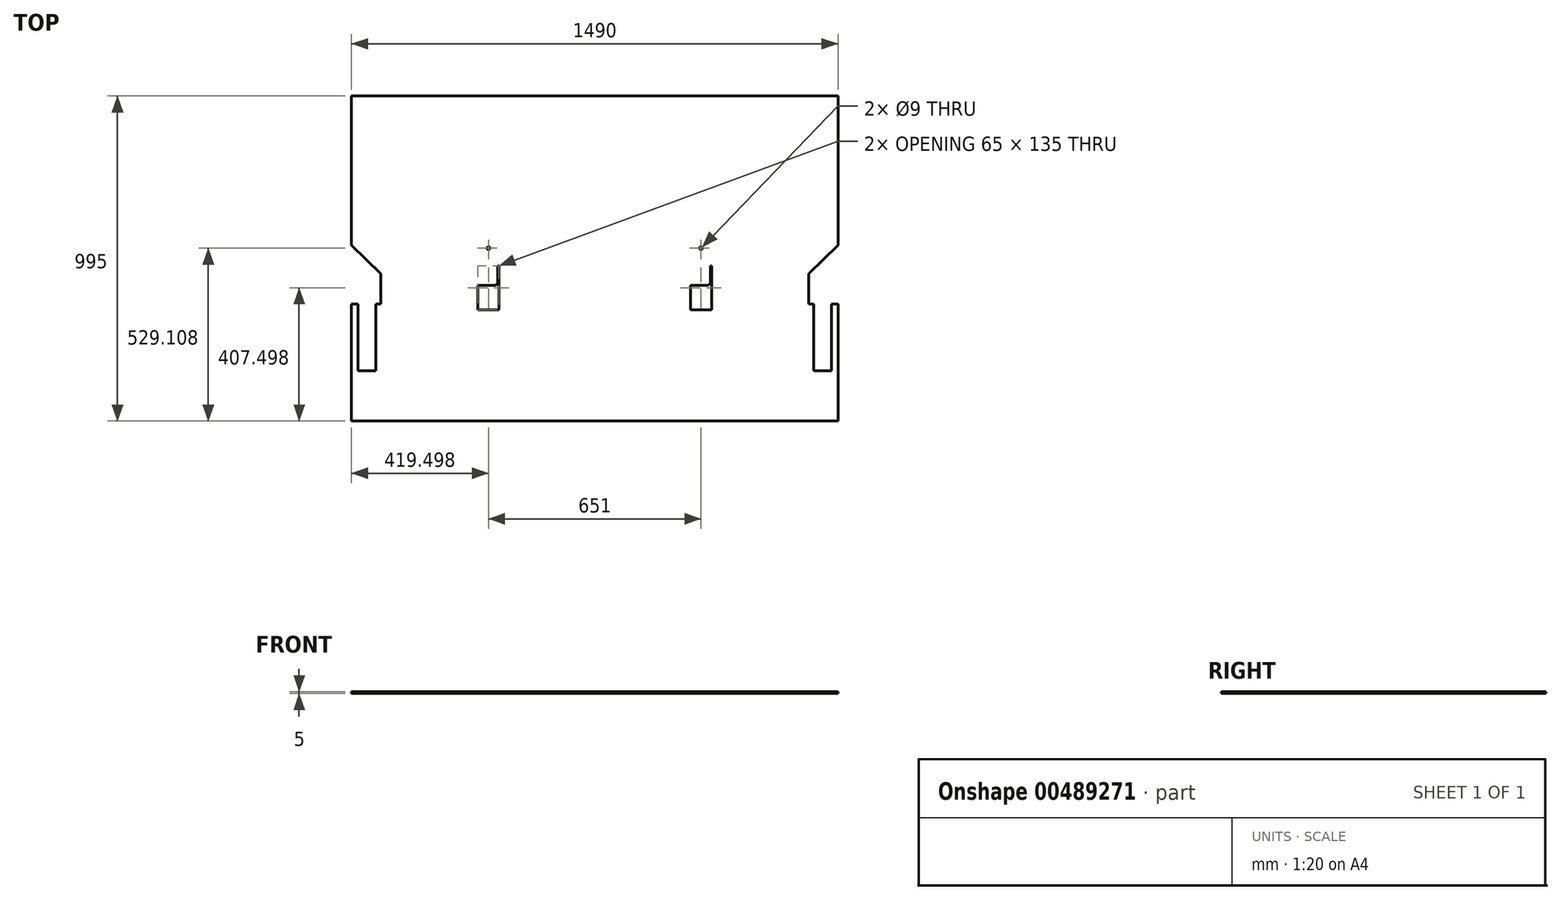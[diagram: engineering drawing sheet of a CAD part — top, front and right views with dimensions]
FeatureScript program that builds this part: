
annotation { "Feature Type Name" : "Feature", "Feature Type Description" : "" }
export const myFeature = defineFeature(function(context is Context, id is Id, definition is map)
    precondition{}
    {
        {
            var Q0;
            Q0=qCreatedBy(makeId("Top.planeOp"),FACE);
            var sketch = newSketch(context, id + "F0", { "sketchPlane" : qUnion([Q0])});
            skLineSegment(sketch, "E0", {"start": v(-764.22, 878.16) * mm, "end": v(725.78, 878.16) * mm});
            skLineSegment(sketch, "E1", {"start": v(725.78, 878.16) * mm, "end": v(725.78, 420.9) * mm});
            skLineSegment(sketch, "E2", {"start": v(725.78, 420.9) * mm, "end": v(635.78, 334.16) * mm});
            skLineSegment(sketch, "E3", {"start": v(635.78, 334.16) * mm, "end": v(635.78, 241.16) * mm});
            skLineSegment(sketch, "E4", {"start": v(635.78, 241.16) * mm, "end": v(650.78, 241.16) * mm});
            skLineSegment(sketch, "E5", {"start": v(650.78, 241.16) * mm, "end": v(650.78, 36.16) * mm});
            skLineSegment(sketch, "E6", {"start": v(650.78, 36.16) * mm, "end": v(705.78, 36.16) * mm});
            skLineSegment(sketch, "E7", {"start": v(705.78, 36.16) * mm, "end": v(705.78, 241.16) * mm});
            skLineSegment(sketch, "E8", {"start": v(705.78, 241.16) * mm, "end": v(725.78, 241.16) * mm});
            skLineSegment(sketch, "E9", {"start": v(725.78, 241.16) * mm, "end": v(725.78, -116.84) * mm});
            skLineSegment(sketch, "E10", {"start": v(725.78, -116.84) * mm, "end": v(-764.22, -116.84) * mm});
            skLineSegment(sketch, "E11", {"start": v(-764.22, -116.84) * mm, "end": v(-764.22, 241.16) * mm});
            skLineSegment(sketch, "E12", {"start": v(-764.22, 241.16) * mm, "end": v(-744.22, 241.16) * mm});
            skLineSegment(sketch, "E13", {"start": v(-744.22, 241.16) * mm, "end": v(-744.22, 36.16) * mm});
            skLineSegment(sketch, "E14", {"start": v(-744.22, 36.16) * mm, "end": v(-689.22, 36.16) * mm});
            skLineSegment(sketch, "E15", {"start": v(-689.22, 36.16) * mm, "end": v(-689.22, 241.16) * mm});
            skLineSegment(sketch, "E16", {"start": v(-689.22, 241.16) * mm, "end": v(-674.22, 241.16) * mm});
            skLineSegment(sketch, "E17", {"start": v(-674.22, 241.16) * mm, "end": v(-674.22, 334.16) * mm});
            skLineSegment(sketch, "E18", {"start": v(-674.22, 334.16) * mm, "end": v(-764.22, 420.9) * mm});
            skLineSegment(sketch, "E19", {"start": v(-764.22, 420.9) * mm, "end": v(-764.22, 878.16) * mm});
            skLineSegment(sketch, "E20.bottom", {"start": v(-377.22, 298.16) * mm, "end": v(-312.22, 298.16) * mm});
            skLineSegment(sketch, "E20.top", {"start": v(-377.22, 223.16) * mm, "end": v(-312.22, 223.16) * mm});
            skLineSegment(sketch, "E20.left", {"start": v(-377.22, 298.16) * mm, "end": v(-377.22, 223.16) * mm});
            skLineSegment(sketch, "E20.right", {"start": v(-312.22, 298.16) * mm, "end": v(-312.22, 223.16) * mm});
            skLineSegment(sketch, "E21.bottom", {"start": v(273.78, 298.16) * mm, "end": v(338.78, 298.16) * mm});
            skLineSegment(sketch, "E21.top", {"start": v(273.78, 223.16) * mm, "end": v(338.78, 223.16) * mm});
            skLineSegment(sketch, "E21.left", {"start": v(273.78, 298.16) * mm, "end": v(273.78, 223.16) * mm});
            skLineSegment(sketch, "E21.right", {"start": v(338.78, 298.16) * mm, "end": v(338.78, 223.16) * mm});
            skLineSegment(sketch, "E22.bottom", {"start": v(-316.22, 358.16) * mm, "end": v(-312.22, 358.16) * mm});
            skLineSegment(sketch, "E22.top", {"start": v(-316.22, 298.16) * mm, "end": v(-312.22, 298.16) * mm});
            skLineSegment(sketch, "E22.left", {"start": v(-316.22, 358.16) * mm, "end": v(-316.22, 298.16) * mm});
            skLineSegment(sketch, "E22.right", {"start": v(-312.22, 358.16) * mm, "end": v(-312.22, 298.16) * mm});
            skLineSegment(sketch, "E23.bottom", {"start": v(334.78, 358.16) * mm, "end": v(338.78, 358.16) * mm});
            skLineSegment(sketch, "E23.top", {"start": v(334.78, 298.16) * mm, "end": v(338.78, 298.16) * mm});
            skLineSegment(sketch, "E23.left", {"start": v(334.78, 358.16) * mm, "end": v(334.78, 298.16) * mm});
            skLineSegment(sketch, "E23.right", {"start": v(338.78, 358.16) * mm, "end": v(338.78, 298.16) * mm});
            skLineSegment(sketch, "E24", {"start": v(-323.22, 298.16) * mm, "end": v(-316.22, 305.16) * mm});
            skLineSegment(sketch, "E25", {"start": v(327.78, 298.16) * mm, "end": v(334.78, 305.16) * mm});
            skCircle(sketch, "E26", {"center": v(-344.72, 412.27) * mm, "radius": 4.5 * mm});
            skPoint(sketch, "E26.centerSnap0", {"position": v(-344.72, 298.16) * mm});
            skCircle(sketch, "E27", {"center": v(306.28, 412.27) * mm, "radius": 4.5 * mm});
            skPoint(sketch, "E27.centerSnap0", {"position": v(306.28, 298.16) * mm});
            skSolve(sketch);
        }
        {
            var Q0;
            Q0 = qSketchRegion(id + "F0", true);
            extrude(context, id + "F1", {"entities" : qUnion([Q0]), "flatOperationType" : FlatOperationType.REMOVE, "offsetDistance" : 25 * mm, "depth" : 5 * mm, "domain" : OperationDomain.MODEL});
        }
    });
